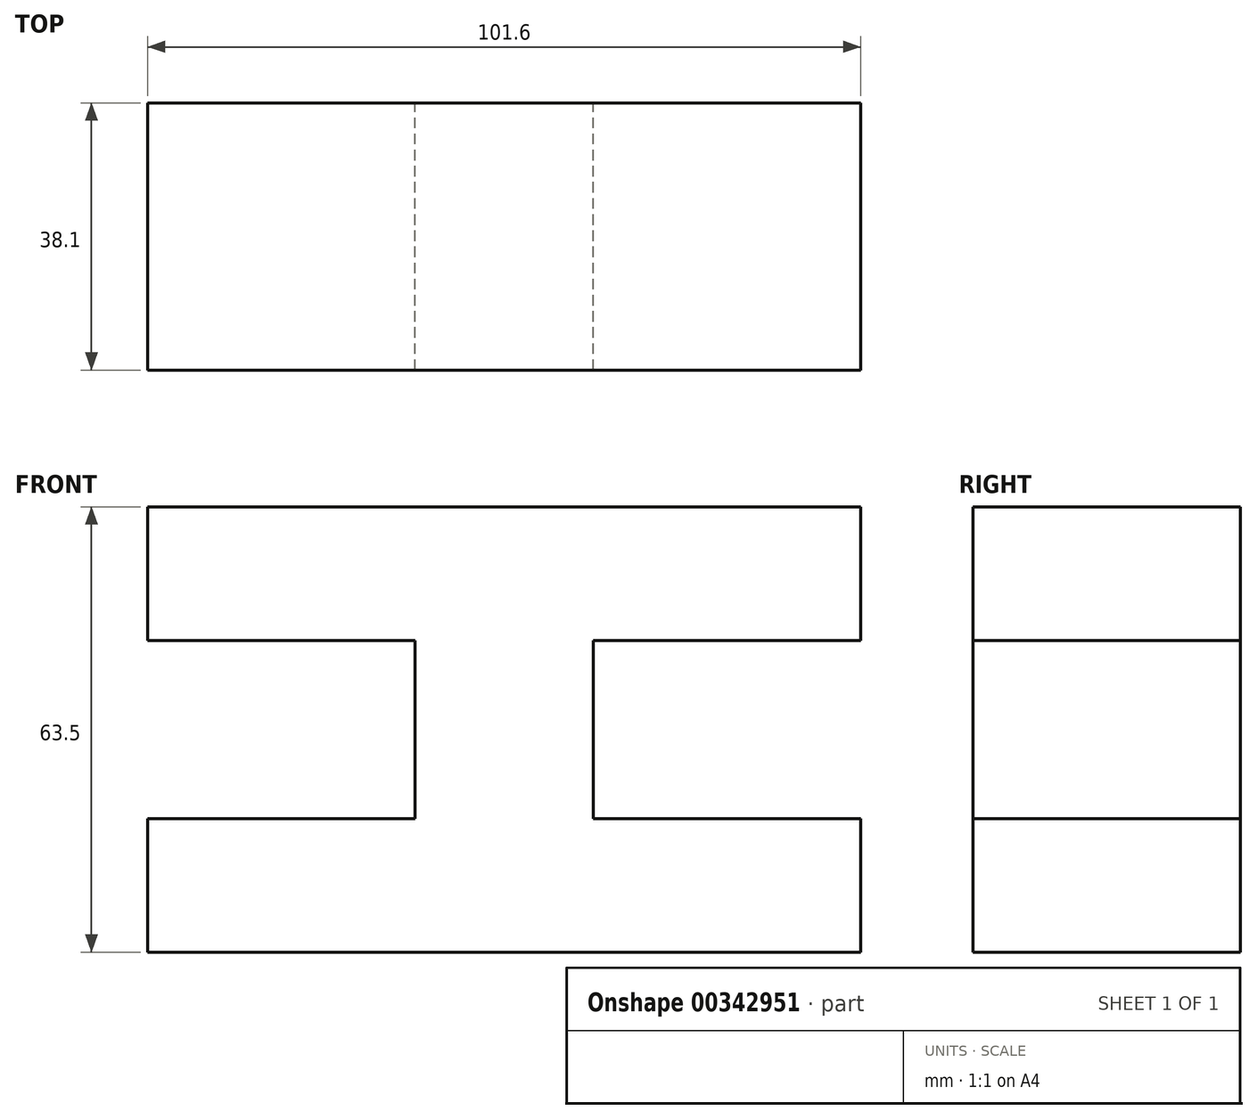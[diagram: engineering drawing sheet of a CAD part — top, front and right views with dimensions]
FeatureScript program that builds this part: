
annotation { "Feature Type Name" : "Feature", "Feature Type Description" : "" }
export const myFeature = defineFeature(function(context is Context, id is Id, definition is map)
    precondition{}
    {
        {
            var Q0;
            Q0=qCreatedBy(makeId("Front.planeOp"),FACE);
            var sketch = newSketch(context, id + "F0", { "sketchPlane" : qUnion([Q0])});
            skLineSegment(sketch, "E0", {"start": v(-54.8, 63.5) * mm, "end": v(46.8, 63.5) * mm});
            skLineSegment(sketch, "E1", {"start": v(-54.8, 63.5) * mm, "end": v(-54.8, 44.45) * mm});
            skLineSegment(sketch, "E2", {"start": v(46.8, 63.5) * mm, "end": v(46.8, 44.45) * mm});
            skLineSegment(sketch, "E3", {"start": v(46.8, 44.45) * mm, "end": v(8.7, 44.45) * mm});
            skLineSegment(sketch, "E4", {"start": v(-54.8, 44.45) * mm, "end": v(-16.7, 44.45) * mm});
            skLineSegment(sketch, "E5", {"start": v(8.7, 44.45) * mm, "end": v(8.7, 19.05) * mm});
            skLineSegment(sketch, "E6", {"start": v(-16.7, 44.45) * mm, "end": v(-16.7, 19.05) * mm});
            skLineSegment(sketch, "E7", {"start": v(-16.7, 19.05) * mm, "end": v(-54.8, 19.05) * mm});
            skLineSegment(sketch, "E8", {"start": v(8.7, 19.05) * mm, "end": v(46.8, 19.05) * mm});
            skLineSegment(sketch, "E9", {"start": v(46.8, 19.05) * mm, "end": v(46.8, 0) * mm});
            skLineSegment(sketch, "E10", {"start": v(-54.8, 19.05) * mm, "end": v(-54.8, 0) * mm});
            skLineSegment(sketch, "E11", {"start": v(-54.8, 0) * mm, "end": v(46.8, 0) * mm});
            skSolve(sketch);
        }
        {
            var Q0;
            Q0 = qSketchRegion(id + "F0", true);
            extrude(context, id + "F1", {"entities" : qUnion([Q0]), "depth" : 38.1 * mm});
        }
    });
